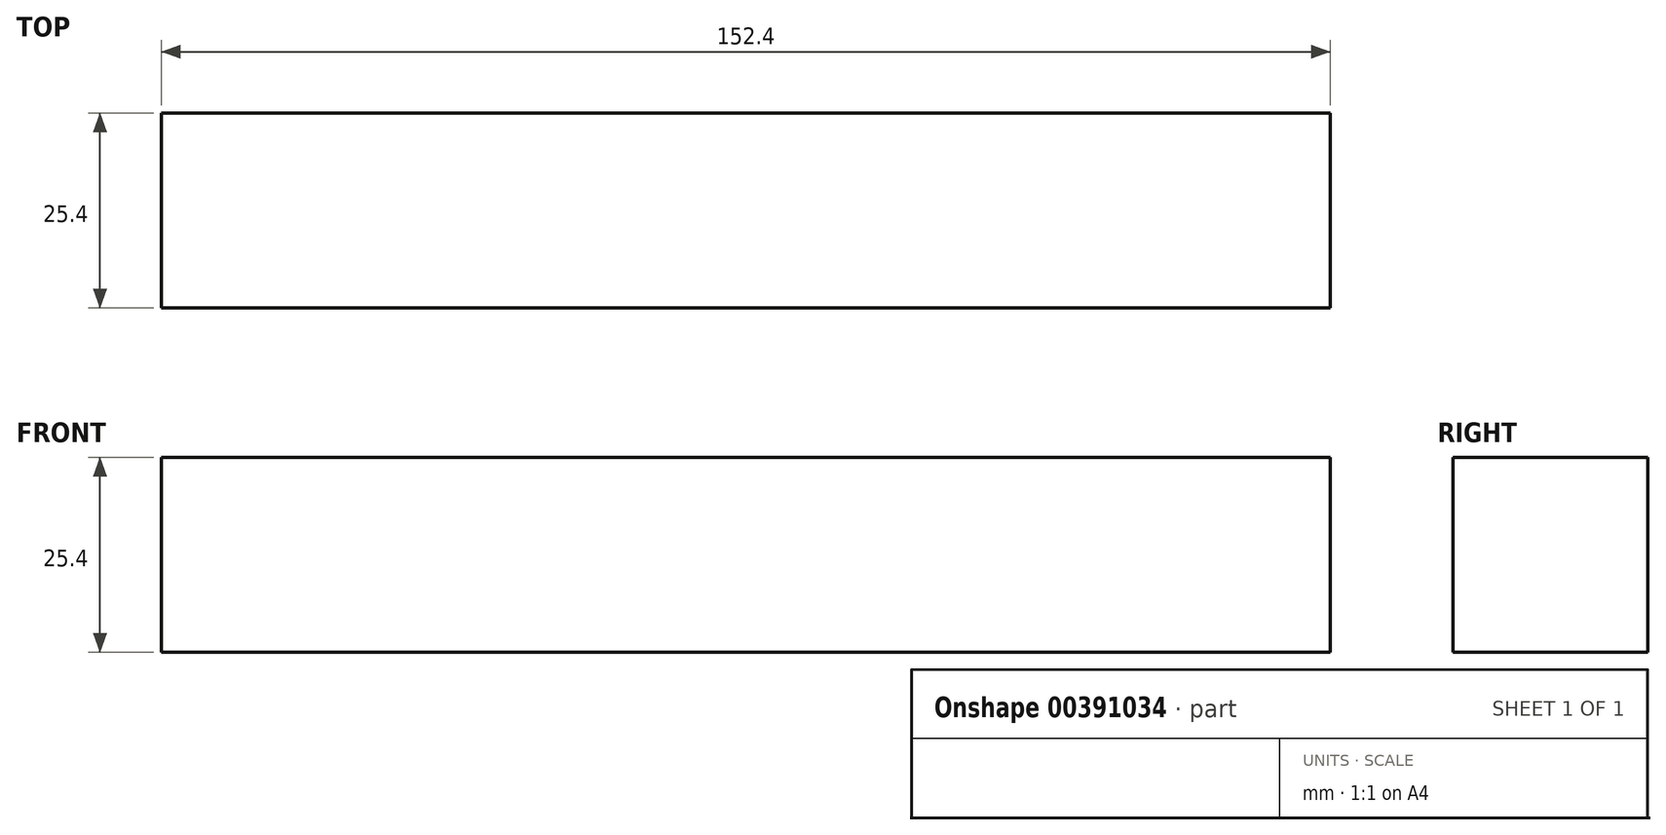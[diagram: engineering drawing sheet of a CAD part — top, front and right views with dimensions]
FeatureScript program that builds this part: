
annotation { "Feature Type Name" : "Feature", "Feature Type Description" : "" }
export const myFeature = defineFeature(function(context is Context, id is Id, definition is map)
    precondition{}
    {
        {
            var Q0;
            Q0=qCreatedBy(makeId("Front.planeOp"),FACE);
            var sketch = newSketch(context, id + "F0", { "sketchPlane" : qUnion([Q0])});
            skLineSegment(sketch, "E0.bottom", {"start": v(-45.17, 0) * mm, "end": v(107.23, 0) * mm});
            skLineSegment(sketch, "E0.top", {"start": v(-45.17, 25.4) * mm, "end": v(107.23, 25.4) * mm});
            skLineSegment(sketch, "E0.left", {"start": v(-45.17, 0) * mm, "end": v(-45.17, 25.4) * mm});
            skLineSegment(sketch, "E0.right", {"start": v(107.23, 0) * mm, "end": v(107.23, 25.4) * mm});
            skSolve(sketch);
        }
        {
            var Q0;
            Q0 = qSketchRegion(id + "F0", true);
            extrude(context, id + "F1", {"entities" : qUnion([Q0]), "depth" : 25.4 * mm});
        }
    });
